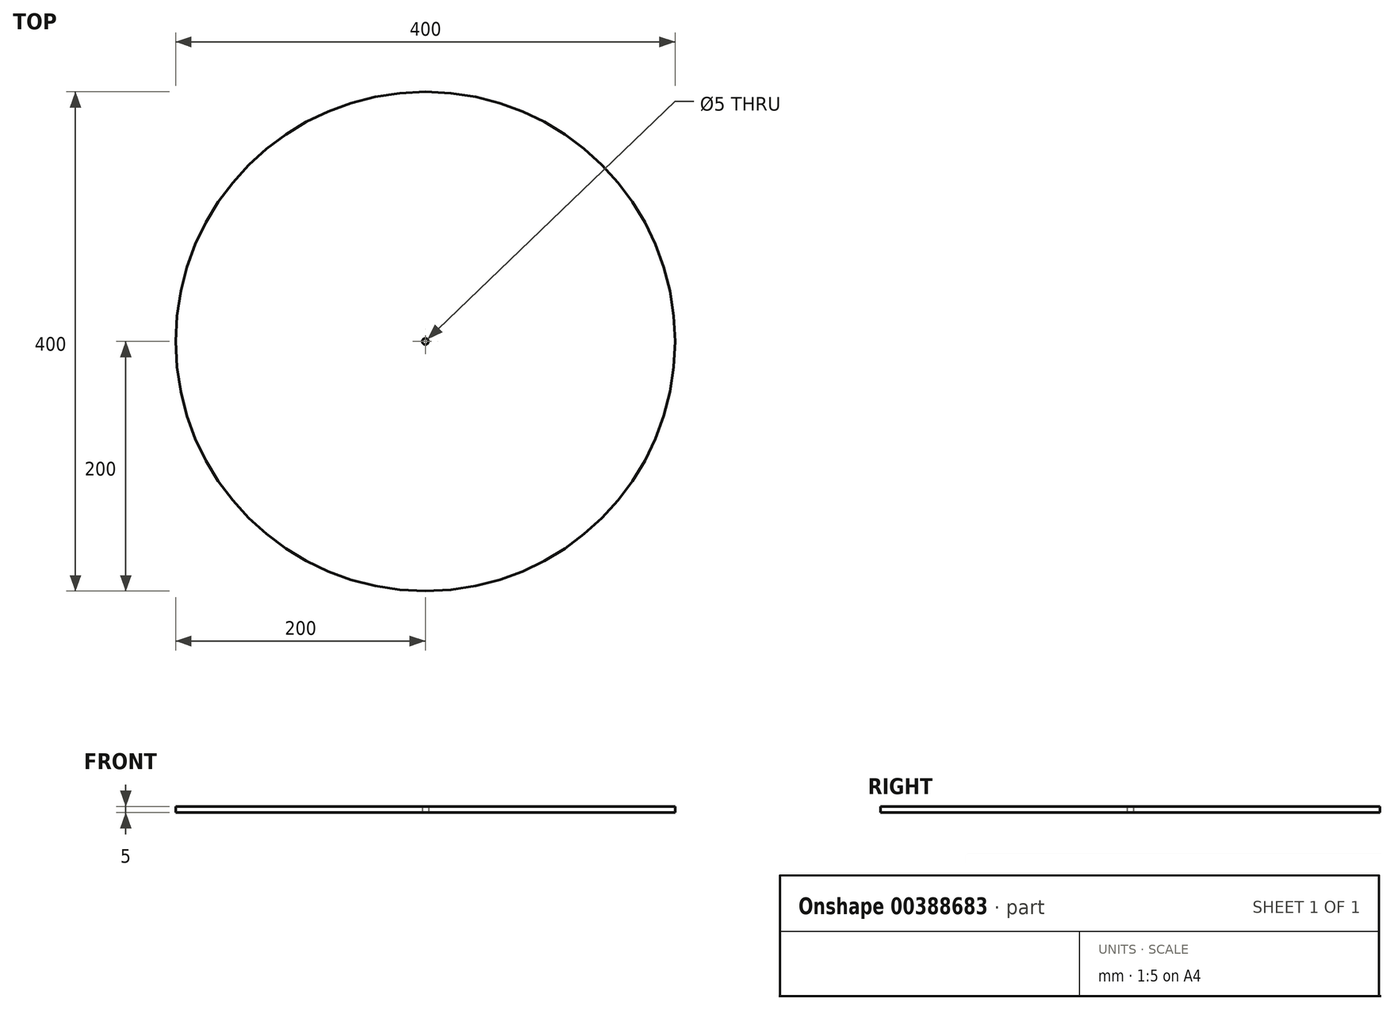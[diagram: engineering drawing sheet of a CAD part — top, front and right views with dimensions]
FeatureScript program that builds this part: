
annotation { "Feature Type Name" : "Feature", "Feature Type Description" : "" }
export const myFeature = defineFeature(function(context is Context, id is Id, definition is map)
    precondition{}
    {
        {
            var Q0;
            Q0=qCreatedBy(makeId("Top.planeOp"),FACE);
            var sketch = newSketch(context, id + "F0", { "sketchPlane" : qUnion([Q0])});
            skCircle(sketch, "E0", {"center": v(0, 0) * mm, "radius": 200 * mm});
            skSolve(sketch);
        }
        {
            var Q0;
            Q0 = qSketchRegion(id + "F0", true);
            extrude(context, id + "F1", {"entities" : qUnion([Q0]), "depth" : 5 * mm});
        }
        {
            var Q0;
            Q0=sQuery(id+"F0.wireOp",VERTEX,"E0.center");
            var Q1;
            Q1=makeQuery(id+"F1.opExtrude","SWEPT_BODY",BODY,{"disambiguationData":[OSD([sQuery(id+"F0.wireOp",EDGE,"E0")])]});
            hole(context, id + "F2", {"style" : HoleStyle.SIMPLE, "endStyle" : HoleEndStyle.THROUGH, "oppositeDirection" : true, "standardTappedOrClearance" : lookupTablePath({ "standard" : "ISO", "size" : "5", "type" : "Drilled" }), "standardBlindInLast" : lookupTablePath({ "standard" : "ISO", "size" : "5", "type" : "Drilled" }), "holeDiameter" : 5 * mm, "isTappedThrough" : true, "tappedDepth" : 12 * mm, "tapClearance" : 3, "locations" : qUnion([Q0]), "scope" : qUnion([Q1])});
        }
    });
